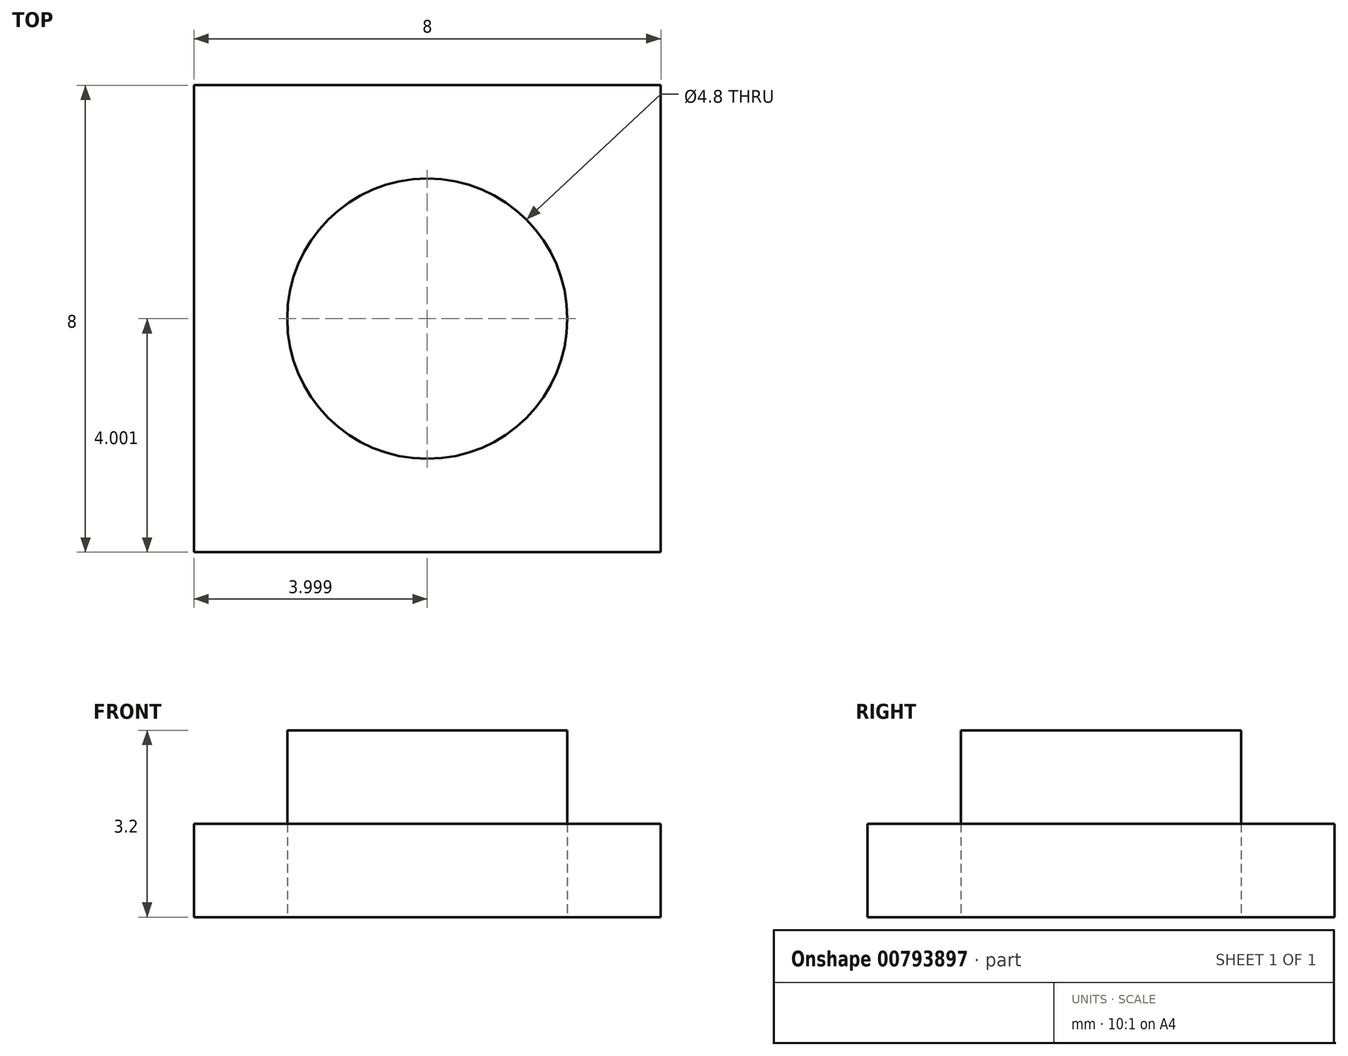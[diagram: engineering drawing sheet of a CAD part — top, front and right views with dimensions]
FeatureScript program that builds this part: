
annotation { "Feature Type Name" : "Feature", "Feature Type Description" : "" }
export const myFeature = defineFeature(function(context is Context, id is Id, definition is map)
    precondition{}
    {
        {
            var Q0;
            Q0=qCreatedBy(makeId("Top.planeOp"),FACE);
            var sketch = newSketch(context, id + "F0", { "sketchPlane" : qUnion([Q0])});
            skCircle(sketch, "E0", {"center": v(-29.2, 17.64) * mm, "radius": 2.4 * mm});
            skLineSegment(sketch, "E1", {"start": v(-29.2, 20.04) * mm, "end": v(-29.2, 15.24) * mm});
            skLineSegment(sketch, "E2.bottom", {"start": v(-33.2, 13.64) * mm, "end": v(-25.2, 13.64) * mm});
            skLineSegment(sketch, "E2.top", {"start": v(-33.2, 21.64) * mm, "end": v(-25.2, 21.64) * mm});
            skLineSegment(sketch, "E2.left", {"start": v(-33.2, 13.64) * mm, "end": v(-33.2, 21.64) * mm});
            skLineSegment(sketch, "E2.right", {"start": v(-25.2, 13.64) * mm, "end": v(-25.2, 21.64) * mm});
            skSolve(sketch);
        }
        {
            var Q0;
            {var subQ0=sQuery(id+"F0.wireOp",EDGE,"E1");Q0=makeQuery(id+"F0.imprint","IMPRINT",FACE,{"disambiguationData":[TD([[makeQuery(id+"F0.imprint","IMPRINT",EDGE,{"derivedFrom":subQ0}),-1.0]])]});}
            var Q1;
            {var subQ0=sQuery(id+"F0.wireOp",EDGE,"E1");Q1=makeQuery(id+"F0.imprint","IMPRINT",FACE,{"disambiguationData":[TD([[makeQuery(id+"F0.imprint","IMPRINT",EDGE,{"derivedFrom":subQ0}),1.0]])]});}
            extrude(context, id + "F1", {"entities" : qUnion([Q0, Q1]), "depth" : 3.2 * mm, "offsetDistance" : 25.4 * mm});
        }
        {
            var Q0;
            Q0=makeQuery(id+"F0.imprint","IMPRINT",FACE,{"disambiguationData":[TD([[makeQuery(id+"F0.imprint","IMPRINT",EDGE,{"derivedFrom":sQuery(id+"F0.wireOp",EDGE,"E2.bottom")}),1.0]])]});
            extrude(context, id + "F2", {"entities" : qUnion([Q0]), "operationType" : NewBodyOperationType.ADD, "depth" : 1.6 * mm, "offsetDistance" : 25.4 * mm});
        }
        {
            var Q0;
            {var subQ0=sQuery(id+"F0.wireOp",EDGE,"E1");Q0=makeQuery(id+"F0.imprint","IMPRINT",FACE,{"disambiguationData":[TD([[makeQuery(id+"F0.imprint","IMPRINT",EDGE,{"derivedFrom":subQ0}),-1.0]])]});}
            var Q1;
            {var subQ0=sQuery(id+"F0.wireOp",EDGE,"E1");Q1=makeQuery(id+"F0.imprint","IMPRINT",FACE,{"disambiguationData":[TD([[makeQuery(id+"F0.imprint","IMPRINT",EDGE,{"derivedFrom":subQ0}),1.0]])]});}
            extrude(context, id + "F3", {"entities" : qUnion([Q0, Q1]), "operationType" : NewBodyOperationType.REMOVE, "depth" : 1.6 * mm, "offsetDistance" : 25.4 * mm});
        }
    });
